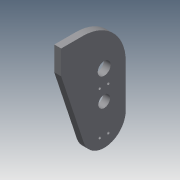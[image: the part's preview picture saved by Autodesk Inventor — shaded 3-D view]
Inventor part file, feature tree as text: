
AUTODESK INVENTOR PART (.ipt)
format: ipt  version: 2013 (Build 170138000, 138)  size: 180,224 bytes
history: native  units: mm
features: extrude x7, sketch x7
ambient origin geometry x8: Origin, YZ Plane, XZ Plane, XY Plane, X Axis, Y Axis, Z Axis, Center Point
bodies: Solid1 (feature_tree)
feature tree (14):
  extrude  "Extrusion1"  Depth=66.3mm
  extrude  "Extrusion2"  Depth=55.0mm
  extrude  "Extrusion3"  Depth=55.0mm
  extrude  "Extrusion4"  Depth=9.9mm
  extrude  "Extrusion5"  Depth=9.9mm
  extrude  "Extrusion6"  Depth=3.0mm
  extrude  "Extrusion7"  Depth=3.0mm
  sketch  "Sketch1"  dims[d0=33.15mm d2=66.3mm]
  sketch  "Sketch2"  dims[d4=18.1mm d5=55.0mm]
  sketch  "Sketch3"  dims[d6=20.0mm d7=55.0mm]
  sketch  "Sketch4"  dims[d8=40.2mm d9=9.9mm]
  sketch  "Sketch5"  dims[d10=9.5mm d11=9.9mm]
  sketch  "Sketch6"  dims[d12=9.5mm d13=3.0mm]
  sketch  "Sketch7"  dims[d14=3.0mm d15=3.0mm d16=3.0mm d17=13.6mm d20=25.0mm d21=45.0mm d22=15.0mm d23=5.0mm d24=0.0mm d25=5.0mm d26=0.0mm d27=25.0mm d28=28.0mm d29=5.0mm d30=0.0mm d31=3.0mm d32=0.0mm d33=40.5mm d34=20.0mm d35=3.0mm d36=0.0mm d37=1.0mm d38=0.0mm d39=10.0mm d40=3.0mm d41=0.0mm]
